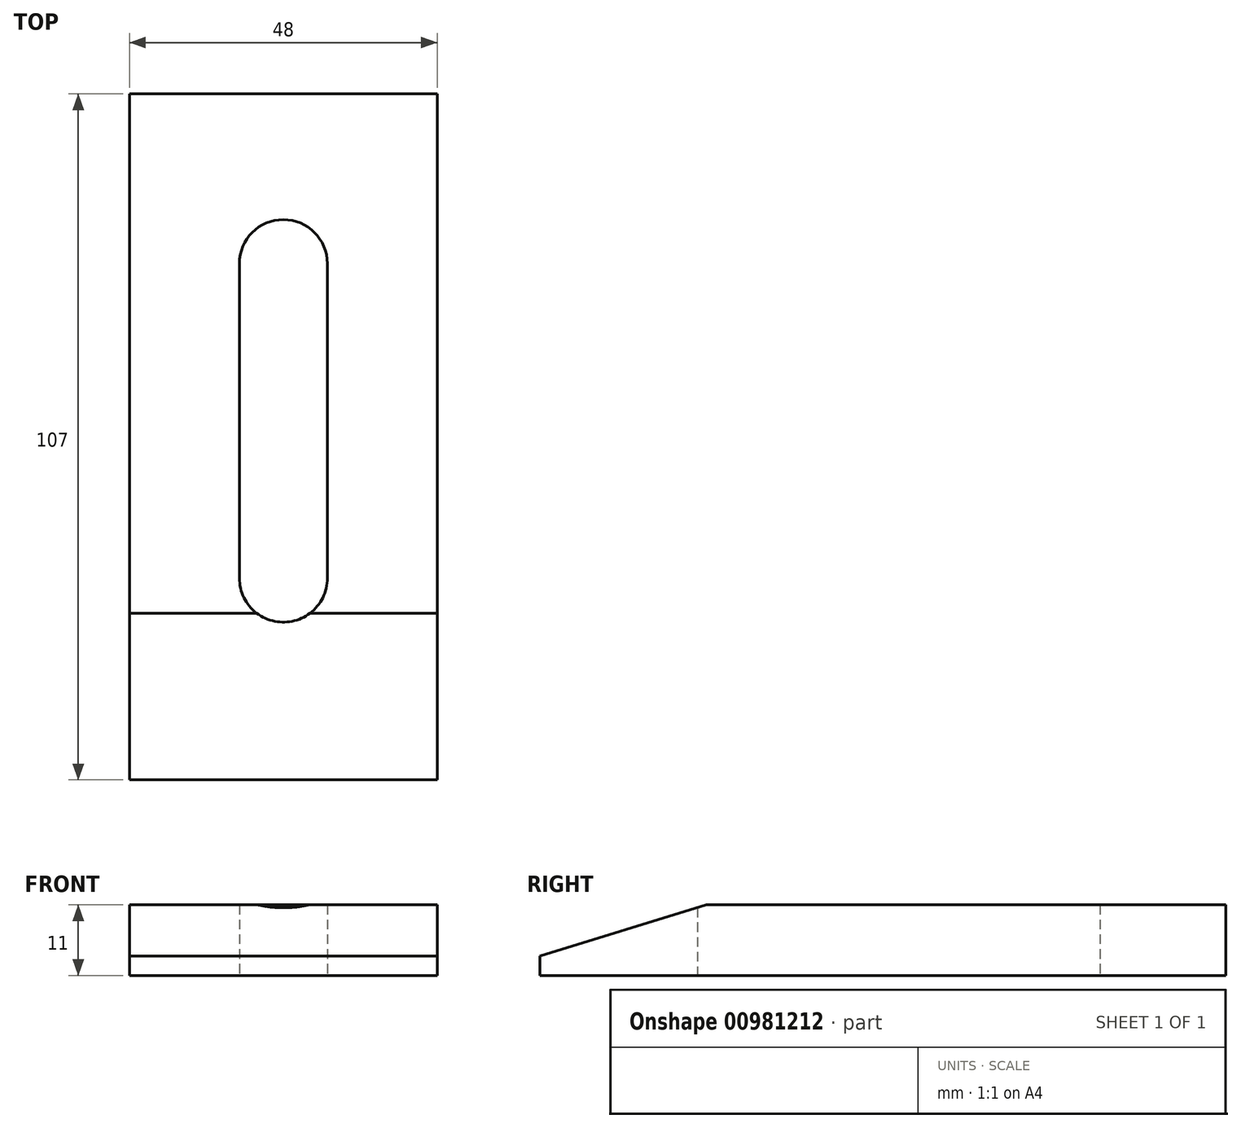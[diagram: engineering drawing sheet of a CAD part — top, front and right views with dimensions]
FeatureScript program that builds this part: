
annotation { "Feature Type Name" : "Feature", "Feature Type Description" : "" }
export const myFeature = defineFeature(function(context is Context, id is Id, definition is map)
    precondition{}
    {
        {
            var Q0;
            Q0=qCreatedBy(makeId("Right.planeOp"),FACE);
            var sketch = newSketch(context, id + "F0", { "sketchPlane" : qUnion([Q0])});
            skLineSegment(sketch, "E0.bottom", {"start": v(-56, 0) * mm, "end": v(51, 0) * mm});
            skLineSegment(sketch, "E0.top", {"start": v(-56, 11) * mm, "end": v(51, 11) * mm});
            skLineSegment(sketch, "E0.left", {"start": v(-56, 0) * mm, "end": v(-56, 11) * mm});
            skLineSegment(sketch, "E0.right", {"start": v(51, 0) * mm, "end": v(51, 11) * mm});
            skLineSegment(sketch, "E1", {"start": v(-56, 3) * mm, "end": v(-30, 11) * mm});
            skSolve(sketch);
        }
        {
            var Q0;
            {var subQ0=sQuery(id+"F0.wireOp",EDGE,"E0.top");var subQ1=sQuery(id+"F0.wireOp",EDGE,"065a0ea0-9919-45ec-b642-3cb09712de05");var subQ2=makeQuery(id+"F0.imprint","INTERSECT",VERTEX,{"disambiguationData":[OD(0.0)],"derivedFrom":[subQ1,subQ0]});Q0=makeQuery(id+"F0.imprint","IMPRINT",FACE,{"disambiguationData":[TD([[makeQuery(id+"F0.imprint","IMPRINT",EDGE,{"disambiguationData":[TD([[subQ2,-1.0]])],"derivedFrom":subQ1}),-1.0]])]});}
            var Q1;
            {var subQ0=sQuery(id+"F0.wireOp",EDGE,"E0.top");var subQ1=sQuery(id+"F0.wireOp",EDGE,"065a0ea0-9919-45ec-b642-3cb09712de05");var subQ2=makeQuery(id+"F0.imprint","INTERSECT",VERTEX,{"disambiguationData":[OD(0.0)],"derivedFrom":[subQ1,subQ0]});Q1=makeQuery(id+"F0.imprint","IMPRINT",FACE,{"disambiguationData":[TD([[makeQuery(id+"F0.imprint","IMPRINT",EDGE,{"disambiguationData":[TD([[subQ2,1.0]])],"derivedFrom":subQ1}),-1.0]])]});}
            var Q2;
            {var subQ4=sQuery(id+"F0.wireOp",EDGE,"E0.right");Q2=makeQuery(id+"F0.imprint","IMPRINT",FACE,{"disambiguationData":[TD([[makeQuery(id+"F0.imprint","IMPRINT",EDGE,{"derivedFrom":subQ4}),1.0]])]});}
            var Q3;
            Q3=makeQuery(id+"F0.imprint","IMPRINT",FACE,{"disambiguationData":[TD([[makeQuery(id+"F0.imprint","IMPRINT",EDGE,{"derivedFrom":sQuery(id+"F0.wireOp",EDGE,"2a3dcd65-8d5c-4f82-8369-24b389055662.bottom")}),-1.0]])]});
            extrude(context, id + "F1", {"entities" : qUnion([Q0, Q1, Q2, Q3]), "depth" : 48 * mm, "offsetDistance" : 25 * mm, "symmetric" : true});
        }
        {
            var Q0;
            Q0=qCreatedBy(makeId("Top.planeOp"),FACE);
            var sketch = newSketch(context, id + "F2", { "sketchPlane" : qUnion([Q0])});
            skLineSegment(sketch, "E2.bottom", {"start": v(6.86, 24.53) * mm, "end": v(-6.86, 24.53) * mm});
            skLineSegment(sketch, "E2.top", {"start": v(6.86, -24.53) * mm, "end": v(-6.86, -24.53) * mm});
            skLineSegment(sketch, "E2.left", {"start": v(6.86, 24.53) * mm, "end": v(6.86, -24.53) * mm});
            skLineSegment(sketch, "E2.right", {"start": v(-6.86, 24.53) * mm, "end": v(-6.86, -24.53) * mm});
            skPoint(sketch, "E2.middle", {"position": v(0, 0) * mm});
            skCircle(sketch, "E3", {"center": v(0, 24.53) * mm, "radius": 6.86 * mm});
            skCircle(sketch, "E4", {"center": v(0, -24.53) * mm, "radius": 6.86 * mm});
            skSolve(sketch);
        }
        {
            var Q0;
            Q0=qSketchRegion(id+"F2",true);
            extrude(context, id + "F3", {"entities" : qUnion([Q0]), "operationType" : NewBodyOperationType.REMOVE, "endBound" : BoundingType.THROUGH_ALL, "depth" : 25 * mm});
        }
        {
            var Q0;
            Q0 = qSketchRegion(id + "F2", true);
            extrude(context, id + "F4", {"entities" : qUnion([Q0]), "operationType" : NewBodyOperationType.REMOVE, "depth" : 25.8 * mm, "offsetDistance" : 25 * mm});
        }
    });
